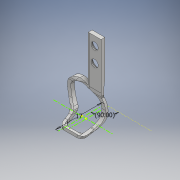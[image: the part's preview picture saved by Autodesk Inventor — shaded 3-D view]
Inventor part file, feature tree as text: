
AUTODESK INVENTOR PART (.ipt)
format: ipt  version: 2018 (Build 220112000, 112)  size: 3,567,616 bytes
history: native  units: mm
features: sketch x154, extrude x143, fillet x57, hole x4, direct_edit x3, other x3
ambient origin geometry x8: Origin, YZ Plane, XZ Plane, XY Plane, X Axis, Y Axis, Z Axis, Center Point
bodies: Body1 (feature_tree), Body2 (feature_tree), Body3 (feature_tree), Body4 (feature_tree), Body5 (feature_tree)
feature tree (364):
  extrude  "Extrusion15"  Depth=18.0mm
  extrude  "Extrusion16"  Depth=1.0mm TaperAngle=0.0deg
  sketch  "Sketch28"  dims[d118=18.7mm d119=0.0mm d120=0.9mm d121=0.0mm]
  extrude  "Extrusion21"  Depth=0.9mm TaperAngle=0.0deg
  extrude  "Extrusion22"  Depth=3.467mm
  extrude  "Extrusion23"  Depth=46.7mm
  hole  "Hole6"  [1 undecoded]
  extrude  "Extrusion27"  Depth=3.467mm
  extrude  "Extrusion28"  Depth=32.03mm
  extrude  "Extrusion30"  Depth=10.0mm TaperAngle=0.0deg
  extrude  "Extrusion31"  Depth=10.0mm
  direct_edit  "Direct Edit1"
  sketch  "Sketch56"  dims[d186=16.3mm d187=0.0mm d188=16.3mm d189=0.0mm]
  sketch  "Sketch57"  dims[d190=16.3mm d191=0.0mm d192=16.3mm d193=0.0mm]
  extrude  "Extrusion33"  Depth=16.3mm TaperAngle=0.0deg
  extrude  "Extrusion34"  Depth=16.3mm TaperAngle=0.0deg
  extrude  "Extrusion35"  Depth=15.9mm TaperAngle=0.0deg
  extrude  "Extrusion36"  Depth=15.9mm TaperAngle=0.0deg
  extrude  "Extrusion37"  Depth=17.0mm
  extrude  "Extrusion38"  Depth=6.0mm TaperAngle=0.0deg
  extrude  "Extrusion39"  Depth=6.0mm TaperAngle=0.0deg
  extrude  "Extrusion40"  Depth=3.17mm
  extrude  "Extrusion41"  Depth=19.4mm
  sketch  "Sketch68"  dims[d249=0.0mm d250=0.0mm d251=10.0mm d252=0.0mm]
  sketch  "Sketch69"  dims[d253=3.91mm d254=0.0mm d255=0.0mm d256=0.0mm]
  extrude  "Extrusion42"  Depth=0.8mm TaperAngle=0.0deg
  extrude  "Extrusion43"  Depth=10.0mm
  extrude  "Extrusion45"  Depth=10.0mm TaperAngle=0.0deg
  extrude  "Extrusion47"  TaperAngle=0.0deg  [1 undecoded]
  extrude  "Extrusion48"  Depth=10.0mm TaperAngle=0.0deg
  extrude  "Extrusion49"  Depth=0.6mm TaperAngle=0.0deg
  direct_edit  "Direct Edit3"
  extrude  "Extrusion51"  Depth=0.199mm
  extrude  "Extrusion52"  TaperAngle=0.0deg  [1 undecoded]
  extrude  "Extrusion53"  Depth=0.7mm TaperAngle=0.0deg
  extrude  "Extrusion54"  Depth=3.64mm
  extrude  "Extrusion55"  Depth=0.09mm TaperAngle=0.0deg
  extrude  "Extrusion57"  Depth=0.356mm
  extrude  "Extrusion60"  Depth=3.9mm TaperAngle=0.0deg
  extrude  "Extrusion61"  Depth=3.9mm TaperAngle=0.0deg
  extrude  "Extrusion62"  Depth=0.886mm
  fillet  "Fillet13"  Radius=3.9mm
  extrude  "Extrusion63"  Depth=10.0mm TaperAngle=0.0deg
  extrude  "Extrusion64"  TaperAngle=0.0deg  [1 undecoded]
  extrude  "Extrusion65"  TaperAngle=0.0deg  [1 undecoded]
  extrude  "Extrusion66"  Depth=0.253mm
  extrude  "Extrusion67"  TaperAngle=0.0deg  [1 undecoded]
  fillet  "Fillet14"  [1 undecoded]
  extrude  "Extrusion68"  Depth=15.0mm
  extrude  "Extrusion69"  Depth=22.68928mm
  extrude  "Extrusion70"  TaperAngle=90.0deg  [1 undecoded]
  fillet  "Fillet15"  [1 undecoded]
  extrude  "Extrusion71"  Depth=0.954mm
  extrude  "Extrusion72"  Depth=3.490659mm
  extrude  "Extrusion73"  Depth=6.0mm TaperAngle=0.0deg
  extrude  "Extrusion74"  Depth=2.0mm TaperAngle=0.0deg
  fillet  "Fillet16"  Radius=2.0mm
  fillet  "Fillet17"  [1 undecoded]
  extrude  "Extrusion75"  Depth=10.0mm
  extrude  "Extrusion77"  Depth=5.0mm TaperAngle=0.0deg
  extrude  "Extrusion78"  Depth=3.8mm
  extrude  "Extrusion79"  Depth=3.213mm
  extrude  "Extrusion80"  Depth=10.0mm TaperAngle=0.0deg
  extrude  "Extrusion81"  Depth=10.0mm TaperAngle=0.0deg
  extrude  "Extrusion82"  Depth=10.0mm TaperAngle=0.0deg
  fillet  "Fillet18"  Radius=10.0mm
  fillet  "Fillet19"  Radius=10.0mm
  fillet  "Fillet20"  Radius=10.0mm
  extrude  "Extrusion83"  Depth=10.0mm TaperAngle=0.0deg
  extrude  "Extrusion84"  TaperAngle=0.0deg  [1 undecoded]
  extrude  "Extrusion85"  Depth=1.49mm
  fillet  "Fillet21"  Radius=0.859mm
  extrude  "Extrusion87"  Depth=0.149mm
  extrude  "Extrusion88"  Depth=1.77mm
  extrude  "Extrusion89"  Depth=10.0mm TaperAngle=0.0deg
  direct_edit  "Direct Edit7"
  extrude  "Extrusion90"  Depth=4.0mm TaperAngle=0.0deg
  extrude  "Extrusion91"  TaperAngle=0.0deg  [1 undecoded]
  fillet  "Fillet27"  [1 undecoded]
  extrude  "Extrusion92"  Depth=7.0mm TaperAngle=0.0deg
  extrude  "Extrusion93"  Depth=10.0mm TaperAngle=0.0deg
  extrude  "Extrusion94"  Depth=7.0mm TaperAngle=0.0deg
  fillet  "Fillet29"  Radius=7.0mm
  hole  "Hole7"  [1 undecoded]
  extrude  "Extrusion95"  Depth=1.7mm TaperAngle=0.0deg
  extrude  "Extrusion97"  Depth=8.713mm
  extrude  "Extrusion98"  Depth=2.6mm
  extrude  "Extrusion99"  TaperAngle=0.0deg  [1 undecoded]
  extrude  "Extrusion100"  Depth=10.0mm TaperAngle=0.0deg
  extrude  "Extrusion101"  Depth=10.0mm TaperAngle=0.0deg
  extrude  "Extrusion102"  TaperAngle=0.0deg  [1 undecoded]
  extrude  "Extrusion103"  Depth=10.0mm TaperAngle=0.0deg
  extrude  "Extrusion104"  TaperAngle=0.0deg  [1 undecoded]
  extrude  "Extrusion105"  Depth=1.64mm
  fillet  "Fillet30"  Radius=0.5mm
  extrude  "Extrusion106"  TaperAngle=0.0deg  [1 undecoded]
  fillet  "Fillet33"  Radius=1.2mm
  fillet  "Fillet34"  Radius=1.2mm
  fillet  "Fillet35"  Radius=1.29mm
  extrude  "Extrusion107"  Depth=10.0mm TaperAngle=0.0deg
  fillet  "Fillet36"  Radius=4.668mm
  fillet  "Fillet37"  Radius=1.4mm
  fillet  "Fillet38"  Radius=25.3mm
  extrude  "Extrusion108"  TaperAngle=0.0deg  [1 undecoded]
  extrude  "Extrusion109"  Depth=25.3mm TaperAngle=0.0deg
  extrude  "Extrusion110"  Depth=0.25mm TaperAngle=0.0deg
  extrude  "Extrusion111"  Depth=2.0mm
  extrude  "Extrusion112"  Depth=2.01mm
  sketch  "Sketch146"  dims[d552=0.25mm d553=0.0mm d554=1.4mm d555=0.0mm]
  extrude  "Extrusion113"  Depth=1.4mm TaperAngle=0.0deg
  extrude  "Extrusion114"  Depth=2.0mm
  extrude  "Extrusion115"  Depth=6.2mm TaperAngle=0.0deg
  extrude  "Extrusion116"  Depth=2.0mm
  extrude  "Extrusion118"  Depth=6.2mm TaperAngle=0.0deg
  sketch  "Sketch154"  dims[d573=5.5mm d574=2.334mm]
  extrude  "Extrusion119"  Depth=2.6mm
  extrude  "Extrusion120"  Depth=2.334mm
  extrude  "Extrusion121"  Depth=3.213mm
  extrude  "Extrusion122"  Depth=10.0mm TaperAngle=0.0deg
  extrude  "Extrusion123"  Depth=2.0mm
  extrude  "Extrusion124"  Depth=10.0mm
  extrude  "Extrusion125"  Depth=12.8mm
  extrude  "Extrusion126"  Depth=10.0mm TaperAngle=0.0deg
  extrude  "Extrusion127"  Depth=8.47mm
  hole  "Hole8"  [1 undecoded]
  extrude  "Extrusion128"  Depth=3.2mm TaperAngle=0.0deg
  extrude  "Extrusion129"  Depth=2.0mm
  extrude  "Extrusion130"  Depth=2.0mm
  extrude  "Extrusion132"  Depth=2.0mm TaperAngle=0.0deg
  extrude  "Extrusion133"  Depth=9.5mm TaperAngle=0.0deg
  extrude  "Extrusion134"  Depth=2.0mm
  extrude  "Extrusion135"  Depth=10.0mm TaperAngle=0.0deg
  extrude  "Extrusion136"  Depth=4.0mm TaperAngle=0.0deg
  extrude  "Extrusion137"  Depth=1.245mm TaperAngle=0.0deg
  extrude  "Extrusion138"  Depth=2.0mm
  extrude  "Extrusion139"  Depth=1.0mm TaperAngle=0.0deg
  extrude  "Extrusion140"  Depth=2.0mm
  sketch  "Sketch182"  dims[d641=1.33mm d642=2.0mm]
  fillet  "Fillet39"  Radius=1.0mm
  extrude  "Extrusion141"  Depth=2.0mm
  extrude  "Extrusion142"  Depth=2.0mm
  sketch  "Sketch185"  dims[d21=1.0mm d22=1.0mm]
  extrude  "Extrusion143"  Depth=2.0mm
  extrude  "Extrusion144"  Depth=2.0mm
  extrude  "Extrusion145"  Depth=1.0mm
  fillet  "Fillet41"  [1 undecoded]
  extrude  "Extrusion146"  [1 undecoded]
  extrude  "Extrusion147"  [1 undecoded]
  extrude  "Extrusion148"  [1 undecoded]
  extrude  "Extrusion149"  [1 undecoded]
  extrude  "Extrusion150"  [1 undecoded]
  extrude  "Extrusion152"  [1 undecoded]
  extrude  "Extrusion153"  [1 undecoded]
  extrude  "Extrusion154"  [1 undecoded]
  extrude  "Extrusion155"  [1 undecoded]
  fillet  "Fillet42"  [1 undecoded]
  fillet  "Fillet43"  [1 undecoded]
  fillet  "Fillet44"  [1 undecoded]
  fillet  "Fillet45"  [1 undecoded]
  extrude  "Extrusion156"  [1 undecoded]
  extrude  "Extrusion157"  [1 undecoded]
  fillet  "Fillet46"  [1 undecoded]
  fillet  "Fillet47"  [1 undecoded]
  fillet  "Fillet48"  [1 undecoded]
  extrude  "Extrusion158"  [1 undecoded]
  extrude  "Extrusion159"  [1 undecoded]
  fillet  "Fillet49"  [1 undecoded]
  extrude  "Extrusion160"  [1 undecoded]
  extrude  "Extrusion162"  [1 undecoded]
  hole  "Hole9"  [1 undecoded]
  sketch  "Sketch205"
  extrude  "Extrusion163"  [1 undecoded]
  fillet  "Fillet50"  [1 undecoded]
  fillet  "Fillet51"  [1 undecoded]
  extrude  "Extrusion164"  [1 undecoded]
  fillet  "Fillet52"  [1 undecoded]
  fillet  "Fillet53"  [1 undecoded]
  fillet  "Fillet54"  [1 undecoded]
  fillet  "Fillet55"  [1 undecoded]
  extrude  "Extrusion165"  [1 undecoded]
  fillet  "Fillet56"  [1 undecoded]
  fillet  "Fillet57"  [1 undecoded]
  extrude  "Extrusion166"  [1 undecoded]
  extrude  "Extrusion167"  [1 undecoded]
  extrude  "Extrusion168"  [1 undecoded]
  extrude  "Extrusion169"  [1 undecoded]
  fillet  "Fillet58"  [1 undecoded]
  fillet  "Fillet59"  [1 undecoded]
  fillet  "Fillet60"  [1 undecoded]
  fillet  "Fillet61"  [1 undecoded]
  fillet  "Fillet62"  [1 undecoded]
  extrude  "Extrusion170"  [1 undecoded]
  extrude  "Extrusion171"  [1 undecoded]
  extrude  "Extrusion172"  [1 undecoded]
  fillet  "Fillet63"  [1 undecoded]
  fillet  "Fillet64"  [1 undecoded]
  fillet  "Fillet65"  [1 undecoded]
  sketch  "Sketch220"
  extrude  "Extrusion173"  [1 undecoded]
  extrude  "Extrusion174"  [1 undecoded]
  extrude  "Extrusion175"  [1 undecoded]
  extrude  "Extrusion176"  [1 undecoded]
  extrude  "Extrusion177"  [1 undecoded]
  fillet  "Fillet66"  [1 undecoded]
  sketch  "Sketch225"
  fillet  "Fillet67"  [1 undecoded]
  fillet  "Fillet68"  [1 undecoded]
  extrude  "Extrusion178"  [1 undecoded]
  fillet  "Fillet69"  [1 undecoded]
  fillet  "Fillet70"  [1 undecoded]
  extrude  "Extrusion179"  [1 undecoded]
  fillet  "Fillet71"  [1 undecoded]
  fillet  "Fillet72"  [1 undecoded]
  fillet  "Fillet73"  [1 undecoded]
  fillet  "Fillet74"  [1 undecoded]
  fillet  "Fillet75"  [1 undecoded]
  fillet  "Fillet76"  [1 undecoded]
  fillet  "Fillet77"  [1 undecoded]
  fillet  "Fillet78"  [1 undecoded]
  sketch  "Sketch26"  dims[d95=7.5mm d96=18.0mm]
  sketch  "Sketch27"  dims[d97=2.3mm d98=0.0mm d101=1.0mm d102=0.0mm]
  sketch  "Sketch41"  dims[d122=0.7mm d123=0.0mm d128=3.467mm]
  sketch  "Sketch42"  dims[d129=3.467mm d130=46.7mm]
  sketch  "Sketch43"  dims[d134=3.467mm d135=4.369mm d136=5.824mm d137=2.0mm d138=14.3117mm d139=6.637mm d140=0.0mm d150=1.5mm d151=0.0mm]
  sketch  "Sketch50"  dims[d152=1.2mm d153=0.0mm d159=3.467mm]
  sketch  "Sketch51"  dims[d161=3.467mm d168=23.3333mm d173=32.03mm]
  sketch  "Sketch53"  dims[d174=16.015mm d175=10.0mm d176=0.0mm]
  sketch  "Sketch54"  dims[d179=0.0mm d180=0.0mm d181=7.5mm d182=10.0mm d183=10.0mm]
  sketch  "Sketch58"  dims[d194=16.3mm d195=0.0mm d196=15.9mm d197=0.0mm]
  sketch  "Sketch60"  dims[d198=15.9mm d199=0.0mm d200=15.9mm d201=0.0mm]
  sketch  "Sketch61"  dims[d202=15.9mm d203=0.0mm d209=17.0mm]
  sketch  "Sketch62"  dims[d210=90.0deg d211=6.0mm d212=0.0mm]
  sketch  "Sketch63"  dims[d213=0.0mm d214=0.0mm d225=6.0mm d226=0.0mm]
  sketch  "Sketch64"  dims[d230=0.2mm d231=0.0mm d232=3.17mm]
  sketch  "Sketch65"  dims[d233=3.17mm d235=19.4mm]
  sketch  "Sketch66"  dims[d236=6.1mm d237=0.8mm d238=0.0mm]
  sketch  "Sketch67"  dims[d239=0.8mm d240=0.0mm d246=9.0mm d247=10.0mm d248=10.0mm]
  sketch  "Sketch70"  dims[d257=3.91mm d258=0.0mm d261=10.0mm d262=0.0mm]
  sketch  "Sketch72"  dims[d267=0.0mm d268=0.0mm d269=0.6mm d270=0.0mm]
  sketch  "Sketch74"  dims[d271=0.0mm d272=0.0mm d273=0.199mm]
  sketch  "Sketch75"  dims[d274=0.7mm d275=0.0mm d276=0.0mm d277=0.0mm]
  sketch  "Sketch76"  dims[d278=0.0mm d279=0.0mm d280=0.7mm d281=0.0mm]
  sketch  "Sketch79"  dims[d282=0.7mm d283=0.0mm d284=3.64mm]
  sketch  "Sketch80"  dims[d285=0.09mm d286=0.0mm d287=0.09mm d288=0.0mm]
  sketch  "Sketch81"  dims[d289=0.0mm d290=0.0mm d291=0.356mm]
  sketch  "Sketch82"  dims[d292=3.9mm d293=0.0mm d294=3.9mm d295=0.0mm]
  sketch  "Sketch83"  dims[d296=0.0mm d297=0.0mm d298=3.9mm d299=0.0mm]
  sketch  "Sketch86"  dims[d300=0.657mm d301=0.886mm d302=3.9mm d303=0.0mm]
  sketch  "Sketch89"  dims[d309=10.0mm d310=0.0mm d313=10.0mm d314=0.0mm]
  sketch  "Sketch90"  dims[d315=10.0mm d316=0.0mm d317=0.0mm d318=0.0mm]
  sketch  "Sketch91"  dims[d319=10.0mm d320=0.0mm d321=0.0mm d322=0.0mm]
  sketch  "Sketch92"  dims[d323=0.467mm d324=0.253mm]
  sketch  "Sketch93"  dims[d325=0.195mm d326=0.0mm d327=0.0mm d328=90.0deg]
  sketch  "Sketch94"  dims[d329=90.0deg d330=15.0mm]
  sketch  "Sketch95"  dims[d332=11.0mm d333=22.68928mm]
  sketch  "Sketch96"  dims[d335=90.0deg d336=90.0deg d337=0.0mm d338=0.0mm]
  sketch  "Sketch97"  dims[d339=15.0mm d342=7.0mm d343=0.0mm d344=0.954mm]
  sketch  "Sketch98"  dims[d350=90.0deg d351=3.490659mm]
  sketch  "Sketch99"  dims[d352=3.490659mm d353=6.0mm d354=0.0mm]
  sketch  "Sketch100"  dims[d362=1.65mm d363=2.0mm d364=0.0mm d365=2.0mm d366=0.0mm]
  sketch  "Sketch101"  dims[d371=8.5mm d372=10.0mm d373=10.0mm d374=0.0mm d375=0.0mm]
  sketch  "Sketch102"  dims[d376=10.0mm d377=0.0mm d378=0.22mm]
  sketch  "Sketch103"  dims[d379=5.1mm d380=0.0mm d381=5.0mm d382=0.0mm]
  sketch  "Sketch104"  dims[d383=5.0mm d384=0.0mm d386=3.8mm]
  sketch  "Sketch105"  dims[d387=2.6mm d388=3.213mm]
  sketch  "Sketch106"  dims[d389=2.975mm]
  sketch  "Sketch107"  dims[d390=2.6mm d391=6.0mm d392=4.4mm d393=2.0mm d394=14.3117mm d395=8.0mm d396=20.594885mm d397=10.0mm d398=0.0mm]
  sketch  "Sketch108"  dims[d401=0.3mm d402=0.0mm d403=10.0mm d404=0.0mm]
  sketch  "Sketch109"  dims[d405=10.0mm d406=0.0mm d407=10.0mm d408=0.0mm d409=10.0mm d410=0.0mm d411=10.0mm d412=0.0mm d413=10.0mm d414=0.0mm]
  sketch  "Sketch110"  dims[d415=10.0mm d416=0.0mm d417=1.0mm d418=0.0mm]
  sketch  "Sketch113"  dims[d419=0.865mm d421=0.0mm d422=0.0mm]
  sketch  "Sketch114"  dims[d424=5.99mm d425=1.49mm d426=0.859mm]
  sketch  "Sketch115"  dims[d427=1.0mm d428=0.0mm d429=0.149mm]
  sketch  "Sketch117"  dims[d430=0.346mm d431=1.77mm]
  sketch  "Sketch118"  dims[d432=10.0mm d433=0.0mm d434=4.0mm d435=0.0mm]
  sketch  "Sketch119"  dims[d436=4.0mm d437=0.0mm d438=4.0mm d439=0.0mm]
  sketch  "Sketch120"  dims[d440=4.0mm d441=0.0mm d442=0.0mm d443=0.0mm d444=0.0mm d445=0.0mm]
  sketch  "Sketch121"  dims[d446=1.0mm d447=0.0mm d448=7.0mm d449=0.0mm]
  sketch  "Sketch122"  dims[d452=7.0mm d453=0.0mm d454=10.0mm d455=0.0mm]
  sketch  "Sketch123"  dims[d456=0.0mm d457=0.0mm d458=7.0mm d459=0.0mm d460=7.0mm d461=0.0mm]
  sketch  "Sketch124"  dims[d462=0.0mm d463=0.0mm d464=7.0mm d465=0.0mm]
  sketch  "Sketch125"  dims[d466=1.7mm d467=0.0mm d468=1.7mm d469=0.0mm]
  sketch  "Sketch126"  dims[d470=5.95mm d471=8.713mm]
  sketch  "Sketch128"  dims[d472=1.403mm d473=0.0mm d474=2.6mm]
  sketch  "Sketch129"  dims[d475=5.5mm]
  sketch  "Sketch130"  dims[d476=2.6mm d477=6.0mm d478=4.4mm d479=2.0mm d480=14.3117mm d481=8.0mm d482=20.594885mm d483=0.0mm d484=0.0mm]
  sketch  "Sketch131"  dims[d485=0.0mm d486=0.0mm d487=10.0mm d488=0.0mm]
  sketch  "Sketch132"  dims[d494=10.0mm d495=0.0mm d496=10.0mm d497=0.0mm]
  sketch  "Sketch133"  dims[d498=10.0mm d499=0.0mm d500=0.0mm d501=0.0mm]
  sketch  "Sketch134"  dims[d502=10.0mm d503=0.0mm d504=3.7mm d505=0.0mm]
  sketch  "Sketch135"  dims[d506=3.7mm d507=0.0mm d508=0.0mm d509=0.0mm]
  sketch  "Sketch136"  dims[d510=0.0mm d511=0.0mm d512=1.64mm d513=0.5mm d514=0.0mm]
  sketch  "Sketch137"  dims[d515=5.0mm d516=0.0mm d517=0.0mm d518=0.0mm d519=1.2mm d520=0.0mm d521=1.2mm d522=0.0mm d524=1.29mm]
  sketch  "Sketch140"  dims[d525=0.0mm d526=0.0mm d527=10.0mm d528=0.0mm d529=4.668mm d530=1.4mm d531=25.3mm d532=0.0mm]
  sketch  "Sketch141"  dims[d533=25.3mm d534=0.0mm d535=0.0mm d536=0.0mm]
  sketch  "Sketch142"  dims[d539=0.0mm d540=0.0mm d541=25.3mm d542=0.0mm]
  sketch  "Sketch143"  dims[d544=0.4mm d545=0.0mm d546=0.25mm d547=0.0mm]
  sketch  "Sketch144"  dims[d548=2.0mm d549=2.0mm]
  sketch  "Sketch145"  dims[d550=2.8mm d551=2.01mm]
  sketch  "Sketch147"  dims[d556=2.0mm d557=2.0mm]
  sketch  "Sketch148"  dims[d558=3.52mm d559=6.2mm d560=0.0mm]
  sketch  "Sketch149"  dims[d561=6.2mm d562=0.0mm d563=2.0mm]
  sketch  "Sketch150"  dims[d564=7.35mm d565=0.0mm d568=6.2mm d569=0.0mm]
  sketch  "Sketch153"  dims[d570=2.6mm d571=2.6mm]
  sketch  "Sketch156"  dims[d575=2.334mm d576=3.213mm]
  sketch  "Sketch157"  dims[d577=2.6mm d578=6.0mm d579=4.4mm d580=2.0mm d581=14.3117mm d582=8.0mm d583=20.594885mm d584=10.0mm d585=0.0mm]
  sketch  "Sketch161"  dims[d586=2.0mm d587=2.28mm]
  sketch  "Sketch162"  dims[d588=10.0mm d589=0.0mm d590=3.95mm]
  sketch  "Sketch163"  dims[d591=9.98mm d592=12.8mm]
  sketch  "Sketch164"  dims[d593=68.9mm d594=10.0mm d595=0.0mm]
  sketch  "Sketch165"  dims[d596=4.18mm d597=8.47mm]
  sketch  "Sketch166"  dims[d598=10.0mm d599=0.0mm d600=3.2mm d601=0.0mm]
  sketch  "Sketch168"  dims[d602=0.0mm d603=0.0mm d604=3.2mm d605=0.0mm]
  sketch  "Sketch169"  dims[d606=2.0mm d607=2.0mm]
  sketch  "Sketch170"  dims[d608=2.0mm d609=2.0mm]
  sketch  "Sketch171"  dims[d610=2.0mm d611=3.2mm d612=0.0mm]
  sketch  "Sketch173"  dims[d613=9.5mm d614=0.0mm d615=9.5mm d616=0.0mm]
  sketch  "Sketch174"  dims[d617=2.0mm d618=2.0mm]
  sketch  "Sketch175"  dims[d619=2.0mm d620=10.0mm d621=0.0mm]
  sketch  "Sketch176"  dims[d622=4.0mm d623=0.0mm d624=4.0mm d625=0.0mm]
  sketch  "Sketch177"  dims[d626=4.0mm d627=0.0mm d628=1.245mm d629=0.0mm]
  sketch  "Sketch178"  dims[d630=2.0mm d631=0.15mm]
  sketch  "Sketch179"  dims[d632=0.279mm d633=1.0mm d634=0.0mm]
  sketch  "Sketch180"  dims[d635=2.0mm d636=2.0mm d637=1.0mm d638=0.0mm]
  sketch  "Sketch181"  dims[d639=2.0mm d640=1.24mm]
  sketch  "Sketch183"  dims[d643=2.0mm d644=2.0mm]
  sketch  "Sketch184"  dims[d645=2.0mm d646=2.0mm]
  sketch  "Sketch186"
  sketch  "Sketch187"
  sketch  "Sketch188"
  sketch  "Sketch189"
  sketch  "Sketch190"
  sketch  "Sketch191"
  sketch  "Sketch192"
  sketch  "Sketch193"
  sketch  "Sketch194"
  sketch  "Sketch195"
  sketch  "Sketch196"
  sketch  "Sketch197"
  sketch  "Sketch199"
  sketch  "Sketch200"
  sketch  "Sketch201"
  sketch  "Sketch202"
  sketch  "Sketch203"
  sketch  "Sketch204"
  sketch  "Sketch207"
  sketch  "Sketch208"
  sketch  "Sketch209"
  sketch  "Sketch210"
  sketch  "Sketch211"
  sketch  "Sketch212"
  sketch  "Sketch213"
  sketch  "Sketch216"
  sketch  "Sketch217"
  sketch  "Sketch218"
  sketch  "Sketch221"
  sketch  "Sketch222"
  sketch  "Sketch223"
  sketch  "Sketch224"
  sketch  "Sketch226"
  sketch  "Sketch227"
  other  "Scale1"
  other  "Scale3"
  other  "Scale7"
note: 91 required parameter values undecoded (feature->parameter linkage not recoverable at this tier; creation-order binding heuristic only, values carry confidence <= 0.55)
